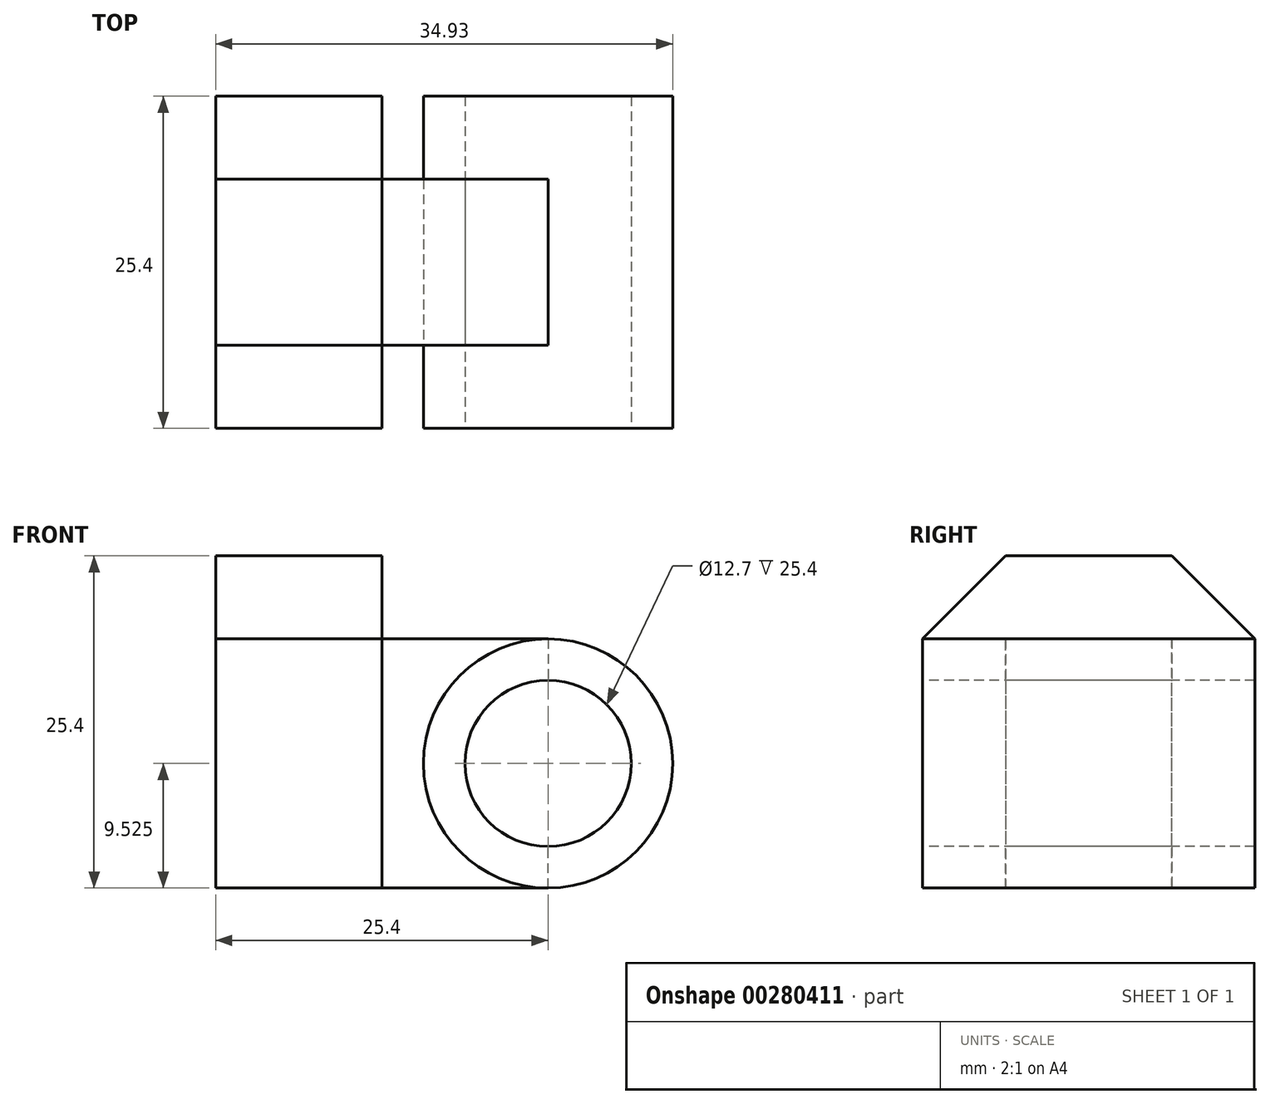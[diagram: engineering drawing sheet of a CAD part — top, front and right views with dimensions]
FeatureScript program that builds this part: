
annotation { "Feature Type Name" : "Feature", "Feature Type Description" : "" }
export const myFeature = defineFeature(function(context is Context, id is Id, definition is map)
    precondition{}
    {
        {
            var Q0;
            Q0=qCreatedBy(makeId("Right.planeOp"),FACE);
            var sketch = newSketch(context, id + "F0", { "sketchPlane" : qUnion([Q0])});
            skLineSegment(sketch, "E0", {"start": v(0, 0) * mm, "end": v(0, 19.05) * mm});
            skLineSegment(sketch, "E1", {"start": v(0, 19.05) * mm, "end": v(6.35, 25.4) * mm});
            skLineSegment(sketch, "E2", {"start": v(6.35, 25.4) * mm, "end": v(19.05, 25.4) * mm});
            skLineSegment(sketch, "E3", {"start": v(19.05, 25.4) * mm, "end": v(25.4, 19.05) * mm});
            skLineSegment(sketch, "E4", {"start": v(25.4, 19.05) * mm, "end": v(25.4, 0) * mm});
            skLineSegment(sketch, "E5", {"start": v(25.4, 0) * mm, "end": v(0, 0) * mm});
            skSolve(sketch);
        }
        {
            var Q0;
            Q0 = qSketchRegion(id + "F0", true);
            extrude(context, id + "F1", {"entities" : qUnion([Q0]), "depth" : 12.7 * mm});
        }
        {
            var Q0;
            Q0=qCreatedBy(makeId("Right.planeOp"),FACE);
            var sketch = newSketch(context, id + "F2", { "sketchPlane" : qUnion([Q0])});
            skLineSegment(sketch, "E6", {"start": v(6.35, 0) * mm, "end": v(6.35, 19.05) * mm});
            skLineSegment(sketch, "E7", {"start": v(6.35, 19.05) * mm, "end": v(19.05, 19.05) * mm});
            skLineSegment(sketch, "E8", {"start": v(19.05, 19.05) * mm, "end": v(19.05, 0) * mm});
            skLineSegment(sketch, "E9", {"start": v(19.05, 0) * mm, "end": v(6.35, 0) * mm});
            skSolve(sketch);
        }
        {
            var Q0;
            Q0 = qSketchRegion(id + "F2", true);
            extrude(context, id + "F3", {"entities" : qUnion([Q0]), "operationType" : NewBodyOperationType.ADD, "depth" : 25.4 * mm});
        }
        {
            var Q0;
            Q0=qCreatedBy(makeId("Front.planeOp"),FACE);
            var sketch = newSketch(context, id + "F4", { "sketchPlane" : qUnion([Q0])});
            skCircle(sketch, "E10", {"center": v(25.4, 9.53) * mm, "radius": 9.53 * mm});
            skSolve(sketch);
        }
        {
            var Q0;
            Q0 = qSketchRegion(id + "F4", true);
            extrude(context, id + "F5", {"entities" : qUnion([Q0]), "oppositeDirection" : true, "depth" : 25.4 * mm});
        }
        {
            var Q0;
            Q0=makeQuery(id+"F5.opExtrude","CAP_FACE",FACE,{"disambiguationData":[OSD([sQuery(id+"F4.wireOp",EDGE,"E10")])],"isStart":true});
            var sketch = newSketch(context, id + "F6", { "sketchPlane" : qUnion([Q0])});
            skCircle(sketch, "E11", {"center": v(25.4, 9.53) * mm, "radius": 6.35 * mm});
            skSolve(sketch);
        }
        {
            var Q0;
            Q0 = qSketchRegion(id + "F6", true);
            extrude(context, id + "F7", {"entities" : qUnion([Q0]), "operationType" : NewBodyOperationType.REMOVE, "oppositeDirection" : true, "depth" : 25.4 * mm});
        }
    });
